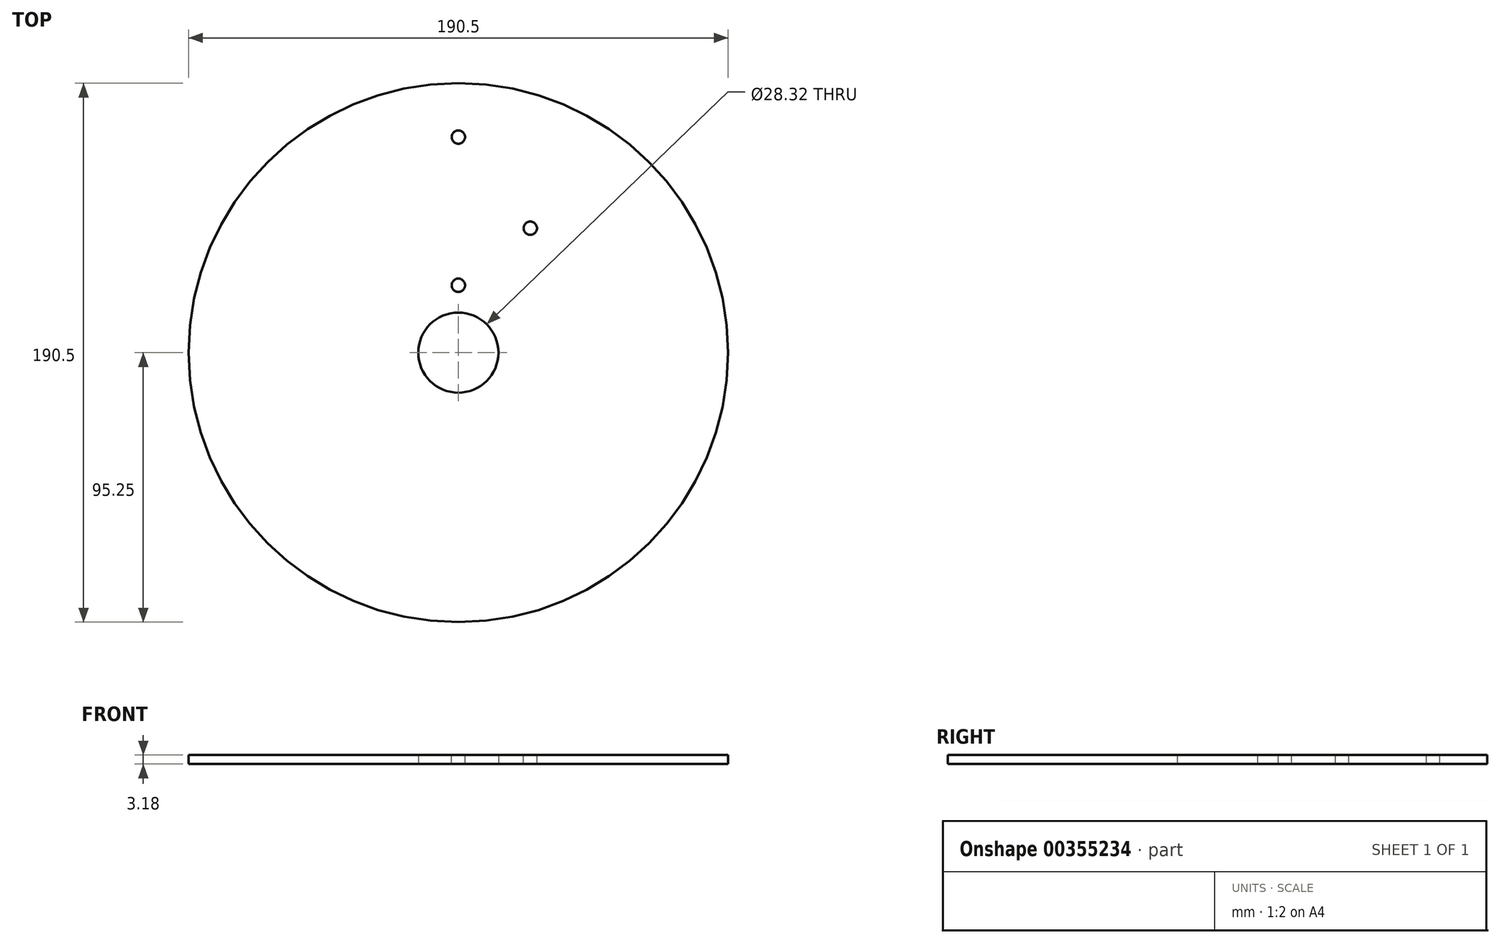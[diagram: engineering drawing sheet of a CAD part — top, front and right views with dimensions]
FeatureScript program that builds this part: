
annotation { "Feature Type Name" : "Feature", "Feature Type Description" : "" }
export const myFeature = defineFeature(function(context is Context, id is Id, definition is map)
    precondition{}
    {
        {
            var Q0;
            Q0=qCreatedBy(makeId("Top.planeOp"),FACE);
            var sketch = newSketch(context, id + "F0", { "sketchPlane" : qUnion([Q0])});
            skCircle(sketch, "E0", {"center": v(0, 0) * mm, "radius": 95.25 * mm});
            skCircle(sketch, "E1", {"center": v(0, 0) * mm, "radius": 14.16 * mm});
            skSolve(sketch);
        }
        {
            var Q0;
            Q0=makeQuery(id+"F0.imprint","IMPRINT",FACE,{"disambiguationData":[TD([[makeQuery(id+"F0.imprint","IMPRINT",EDGE,{"derivedFrom":sQuery(id+"F0.wireOp",EDGE,"E0")}),1.0]])]});
            extrude(context, id + "F1", {"entities" : qUnion([Q0]), "depth" : 3.17 * mm});
        }
        {
            var Q0;
            Q0=makeQuery(id+"F1.opExtrude","CAP_FACE",FACE,{"disambiguationData":[OSD([sQuery(id+"F0.wireOp",EDGE,"E0"),sQuery(id+"F0.wireOp",EDGE,"E1")])],"isStart":false});
            var sketch = newSketch(context, id + "F2", { "sketchPlane" : qUnion([Q0])});
            skCircle(sketch, "E2", {"center": v(0, 23.81) * mm, "radius": 2.36 * mm});
            skCircle(sketch, "E3", {"center": v(0, 76.2) * mm, "radius": 2.36 * mm});
            skCircle(sketch, "E4", {"center": v(25.4, 44) * mm, "radius": 2.36 * mm});
            skLineSegment(sketch, "E5", {"start": v(0, 0) * mm, "end": v(25.4, 44) * mm, "construction": true});
            skSolve(sketch);
        }
        {
            var Q0;
            Q0=qSketchRegion(id+"F2",true);
            extrude(context, id + "F3", {"entities" : qUnion([Q0]), "operationType" : NewBodyOperationType.REMOVE, "endBound" : BoundingType.THROUGH_ALL, "oppositeDirection" : true, "depth" : 25.4 * mm});
        }
    });
